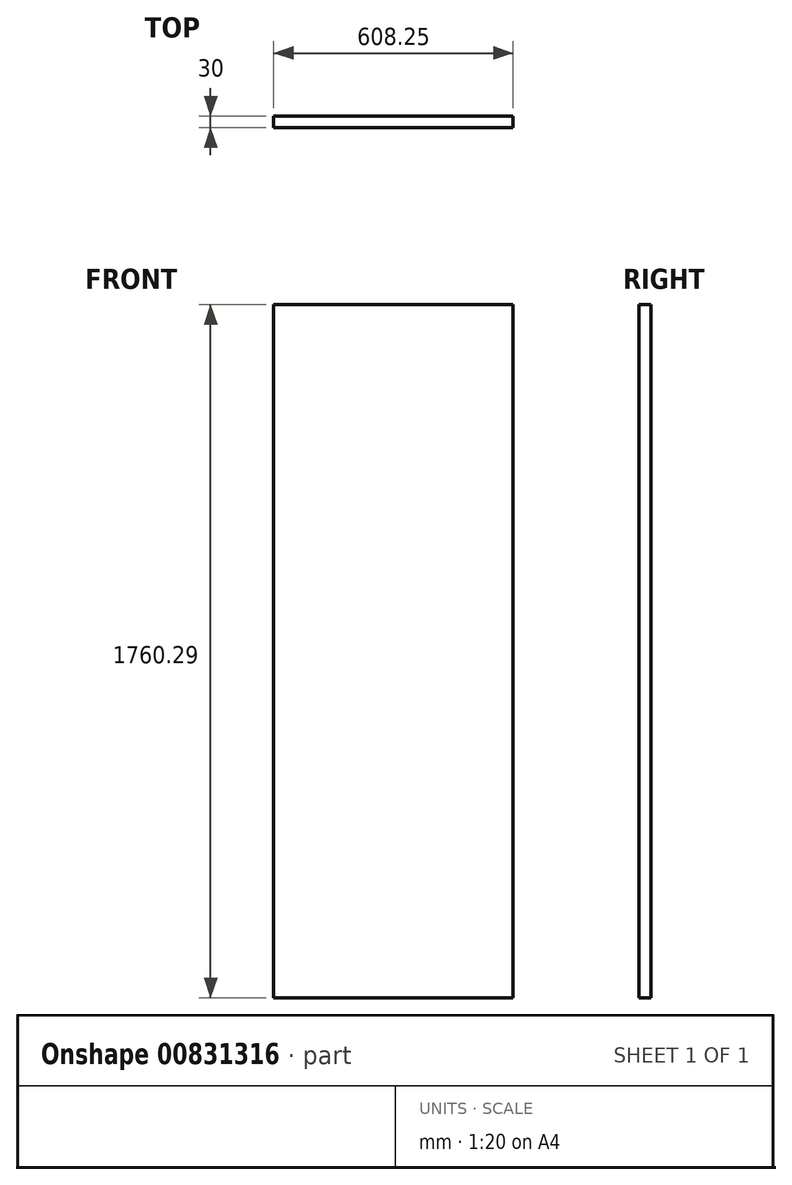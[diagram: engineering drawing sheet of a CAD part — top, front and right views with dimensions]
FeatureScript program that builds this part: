
annotation { "Feature Type Name" : "Feature", "Feature Type Description" : "" }
export const myFeature = defineFeature(function(context is Context, id is Id, definition is map)
    precondition{}
    {
        {
            var Q0;
            Q0=qCreatedBy(makeId("Front.planeOp"),FACE);
            var sketch = newSketch(context, id + "F0", { "sketchPlane" : qUnion([Q0])});
            skLineSegment(sketch, "E0", {"start": v(-2348.34, -1335.91) * mm, "end": v(-1740.09, -1335.91) * mm});
            skLineSegment(sketch, "E1", {"start": v(-1740.09, -1335.91) * mm, "end": v(-1740.09, 424.38) * mm});
            skLineSegment(sketch, "E2", {"start": v(-2348.34, -1335.91) * mm, "end": v(-2348.34, 424.38) * mm});
            skLineSegment(sketch, "E3", {"start": v(-2348.34, 424.38) * mm, "end": v(-1740.09, 424.38) * mm});
            skSolve(sketch);
        }
        {
            var Q0;
            Q0=makeQuery(id+"F0.imprint","IMPRINT",FACE,{"disambiguationData":[TD([[makeQuery(id+"F0.imprint","IMPRINT",EDGE,{"derivedFrom":sQuery(id+"F0.wireOp",EDGE,"E0")}),1.0]])]});
            extrude(context, id + "F1", {"entities" : qUnion([Q0]), "depth" : 30 * mm, "offsetDistance" : 25 * mm});
        }
    });
